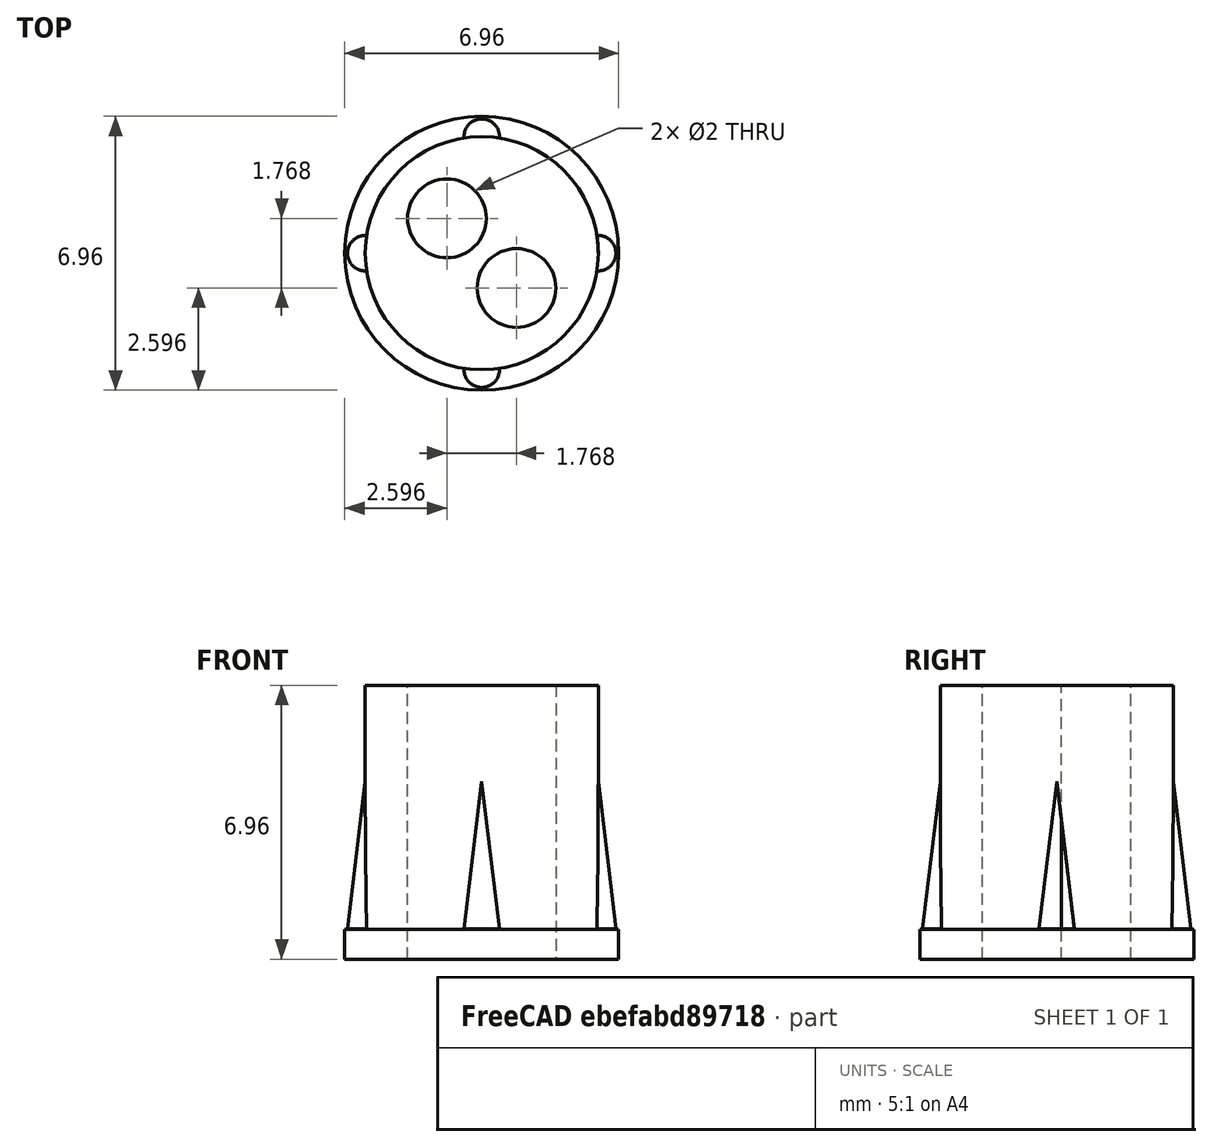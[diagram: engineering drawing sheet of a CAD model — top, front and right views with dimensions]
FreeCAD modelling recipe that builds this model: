
FCSTD DOCUMENT  (FreeCAD 0.15R4671 (Git))
Label: LED_holder_plug
License: All rights reserved
LicenseURL: http://en.wikipedia.org/wiki/All_rights_reserved
objects: Part::Cylinder×2, Part::MultiFuse×2, Part::Cone×1, Part::FeaturePython×1, Sketcher::SketchObject×1, PartDesign::Pocket×1, Part::MultiCommon×1
note: 10 computed .brp shape members not serialized (recipe doc carries the construction recipe); baked Part::Feature solids carry a one-line shape summary decoded from their .brp

FEATURE [Part::Cylinder] Cylinder
  Angle = 360
  Height = 6.2
  Radius = 2.96
FEATURE [Part::Cylinder] Cylinder001
  Angle = 360
  Height = 0.76
  Placement = pos=(0,0,-0.76) rot=(0,0,1;0rad)
  Radius = 3.48
FEATURE [Part::Cone] Cone
  Angle = 360
  Height = 3.75
  Placement = pos=(2.96,0,3.76) rot=(1,0,0;3.14159rad)
  Radius1 = 0
  Radius2 = 0.45
FEATURE [Part::FeaturePython] Array  # Draft array (typed FeaturePython)
  Angle = 360
  ArrayType = 1
  Axis = (0,0,1)
  Base = -> Cone
  Center = (0,0,0)
  Fuse = false
  IntervalAxis = (0,0,0)
  IntervalX = (1,0,0)
  IntervalY = (0,1,0)
  IntervalZ = (0,0,0)
  NumberPolar = 4
  NumberX = 2
  NumberY = 2
  NumberZ = 1
FEATURE [Part::MultiFuse] Fusion
  Shapes = -> [Cylinder,Array]
FEATURE [Part::MultiFuse] Fusion001
  Shapes = -> [Cylinder001,Fusion]
FEATURE [Sketcher::SketchObject] Sketch
  ExternalGeometry = -> [Fusion001]
  Placement = pos=(0,0,6.2) rot=(0,0,1;0rad)
  Support = -> Fusion001 [Face8]
  sketch-geometry (4):
    g0: LineSegment [constr] StartX=-2.09304 StartY=2.09304 StartZ=0 EndX=2.09304 EndY=-2.09304 EndZ=0
    g1: LineSegment [constr] StartX=-2.09304 StartY=-2.09304 StartZ=0 EndX=2.09304 EndY=2.09304 EndZ=0
    g2: Circle CenterX=-0.883883 CenterY=0.883883 CenterZ=0 NormalX=0 NormalY=0 NormalZ=1 Radius=1
    g3: Circle CenterX=0.883883 CenterY=-0.883883 CenterZ=0 NormalX=0 NormalY=0 NormalZ=1 Radius=1
  constraints (14):
    c: PointOnObject(g0,g-3)
    c: PointOnObject(g0,g-3)
    c: PointOnObject(g-1,g0)
    c: PointOnObject(g1,g-3)
    c: PointOnObject(g1,g-3)
    c: PointOnObject(g-1,g1)
    c: Angle(g-2,g0) = 0.785398
    c: Angle(g1,g-2) = 0.785398
    c: PointOnObject(g2,g0)
    c: PointOnObject(g3,g0)
    c: Symmetric(g2,g3,g1)
    c: Equal(g2,g3)
    c: Distance(g2,g3) = 2.5
    c: Radius(g3) = 1
FEATURE [PartDesign::Pocket] Pocket
  Length = 5
  Sketch = -> Sketch
  Type = 1
FEATURE [Part::MultiCommon] Common
  Shapes = -> [Pocket,Fusion001]
